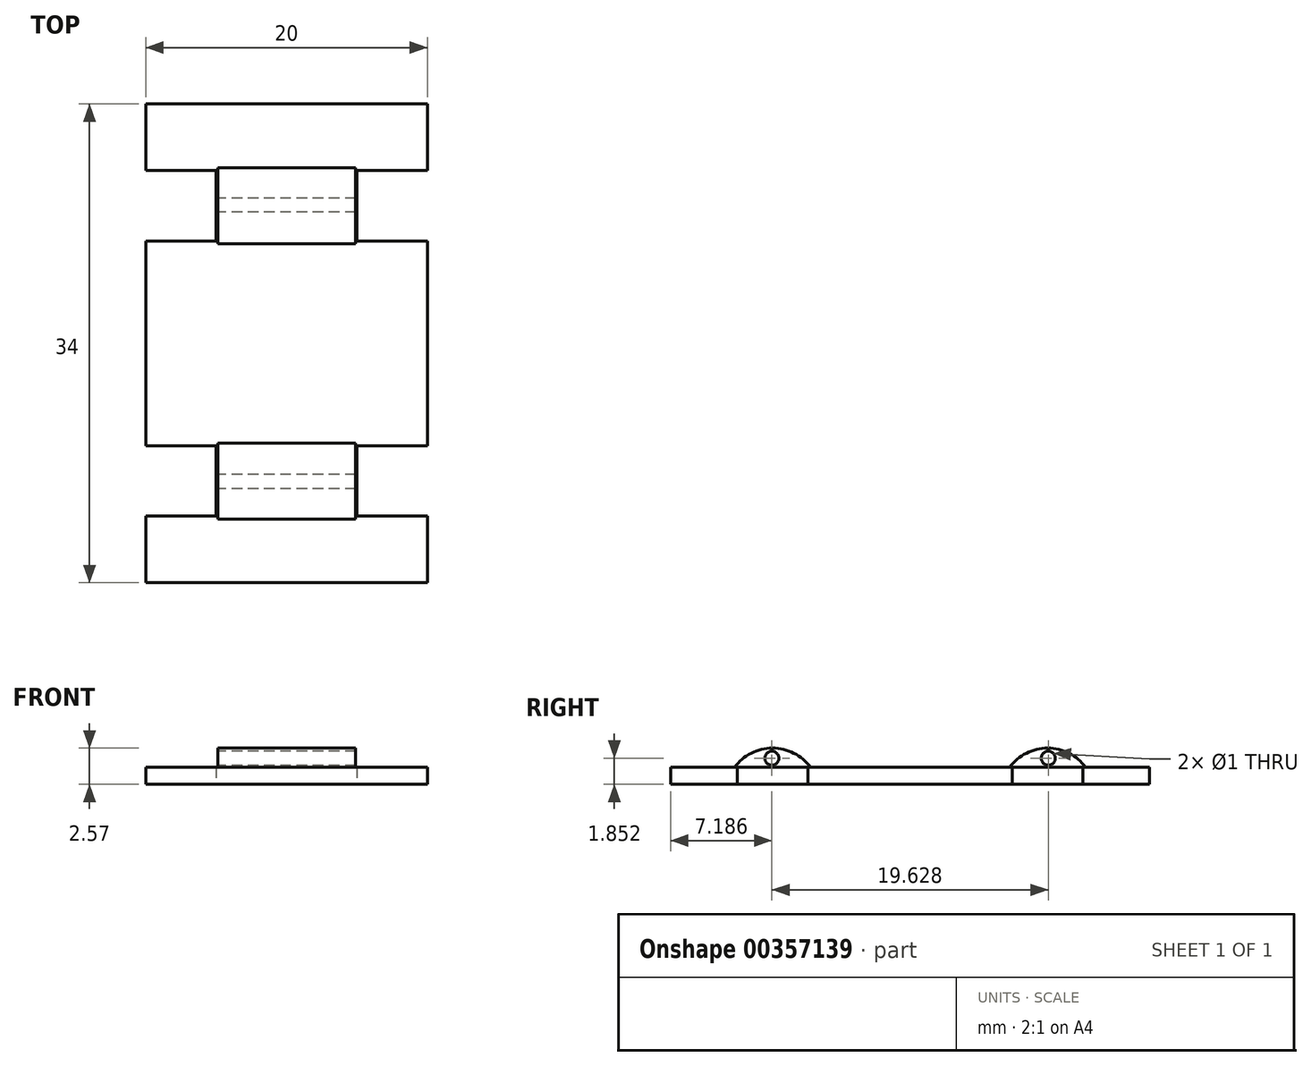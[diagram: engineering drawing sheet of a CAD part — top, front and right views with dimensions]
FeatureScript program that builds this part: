
annotation { "Feature Type Name" : "Feature", "Feature Type Description" : "" }
export const myFeature = defineFeature(function(context is Context, id is Id, definition is map)
    precondition{}
    {
        {
            var Q0;
            Q0=qCreatedBy(makeId("Top.planeOp"),FACE);
            var sketch = newSketch(context, id + "F0", { "sketchPlane" : qUnion([Q0])});
            skLineSegment(sketch, "E0.bottom", {"start": v(10, 17) * mm, "end": v(-10, 17) * mm});
            skLineSegment(sketch, "E0.top", {"start": v(10, -17) * mm, "end": v(-10, -17) * mm});
            skLineSegment(sketch, "E0.left", {"start": v(10, 17) * mm, "end": v(10, 12.27) * mm});
            skLineSegment(sketch, "E0.right", {"start": v(-10, 17) * mm, "end": v(-10, 12.27) * mm});
            skPoint(sketch, "E0.middle", {"position": v(0, 0) * mm});
            skLineSegment(sketch, "E1.bottom", {"start": v(-10, 12.27) * mm, "end": v(-5, 12.27) * mm});
            skLineSegment(sketch, "E1.top", {"start": v(-10, 7.27) * mm, "end": v(-5, 7.27) * mm});
            skLineSegment(sketch, "E1.right", {"start": v(-5, 12.27) * mm, "end": v(-5, 7.27) * mm});
            skLineSegment(sketch, "E2.MirrorCS", {"start": v(5, 12.27) * mm, "end": v(5, 7.27) * mm});
            skLineSegment(sketch, "E3.MirrorCS", {"start": v(10, 12.27) * mm, "end": v(5, 12.27) * mm});
            skLineSegment(sketch, "E4.MirrorCS", {"start": v(10, 7.27) * mm, "end": v(5, 7.27) * mm});
            skLineSegment(sketch, "E5.MirrorCS", {"start": v(-10, -7.27) * mm, "end": v(-5, -7.27) * mm});
            skLineSegment(sketch, "E6.MirrorCS", {"start": v(-5, -12.27) * mm, "end": v(-5, -7.27) * mm});
            skLineSegment(sketch, "E7.MirrorCS", {"start": v(-10, -12.27) * mm, "end": v(-5, -12.27) * mm});
            skLineSegment(sketch, "E8.MirrorCS", {"start": v(10, -7.27) * mm, "end": v(5, -7.27) * mm});
            skLineSegment(sketch, "E9.MirrorCS", {"start": v(5, -12.27) * mm, "end": v(5, -7.27) * mm});
            skLineSegment(sketch, "E10.MirrorCS", {"start": v(10, -12.27) * mm, "end": v(5, -12.27) * mm});
            skLineSegment(sketch, "E11.trimOffspring", {"start": v(-10, 7.27) * mm, "end": v(-10, -7.27) * mm});
            skLineSegment(sketch, "E12.trimOffspring", {"start": v(-10, -12.27) * mm, "end": v(-10, -17) * mm});
            skLineSegment(sketch, "E13.trimOffspring", {"start": v(10, -12.27) * mm, "end": v(10, -17) * mm});
            skLineSegment(sketch, "E14.trimOffspring", {"start": v(10, 7.27) * mm, "end": v(10, -7.27) * mm});
            skSolve(sketch);
        }
        {
            var Q0;
            Q0=makeQuery(id+"F0.imprint","IMPRINT",FACE,{"disambiguationData":[TD([[makeQuery(id+"F0.imprint","IMPRINT",EDGE,{"derivedFrom":sQuery(id+"F0.wireOp",EDGE,"E0.bottom")}),1.0]])]});
            extrude(context, id + "F1", {"entities" : qUnion([Q0]), "endBound" : BoundingType.SYMMETRIC, "depth" : 1.2 * mm});
        }
        {
            var Q0;
            Q0=qCreatedBy(makeId("Right.planeOp"),FACE);
            var sketch = newSketch(context, id + "F2", { "sketchPlane" : qUnion([Q0])});
            skArc(sketch, "E15", {"start": v(-7.04, 0.56) * mm, "mid": v(-9.76, 1.97) * mm, "end": v(-12.49, 0.58) * mm});
            skCircle(sketch, "E16", {"center": v(-9.81, 1.25) * mm, "radius": 0.5 * mm});
            skLineSegment(sketch, "E17", {"start": v(-12.49, 0.58) * mm, "end": v(-7.04, 0.56) * mm});
            skArc(sketch, "E18.MirrorCS", {"start": v(7.04, 0.56) * mm, "mid": v(9.76, 1.97) * mm, "end": v(12.49, 0.58) * mm});
            skLineSegment(sketch, "E19.MirrorCS", {"start": v(12.49, 0.58) * mm, "end": v(7.04, 0.56) * mm});
            skCircle(sketch, "E20.MirrorC", {"center": v(9.81, 1.25) * mm, "radius": 0.5 * mm});
            skSolve(sketch);
        }
        {
            var Q0;
            Q0 = qSketchRegion(id + "F2", true);
            extrude(context, id + "F3", {"entities" : qUnion([Q0]), "operationType" : NewBodyOperationType.ADD, "endBound" : BoundingType.SYMMETRIC, "depth" : 9.8 * mm});
        }
    });
